FCSTD DOCUMENT  (FreeCAD 0.21R33771 (Git))
Label: mount_on_post
License: All rights reserved
LicenseURL: https://en.wikipedia.org/wiki/All_rights_reserved
objects: App::Link×3, App::DocumentObjectGroup×2, PartDesign::CoordinateSystem×2, App::FeaturePython×1, App::Part×1
note: 2 computed .brp shape members not serialized (recipe doc carries the construction recipe); baked Part::Feature solids carry a one-line shape summary decoded from their .brp
EXTERNAL_REF file=../optomech/postasm/post/RS05P.FCStd obj=LCS_foot
EXTERNAL_REF file=../optomech/postasm/post/RS05P.FCStd obj=Part
EXTERNAL_REF file=../optomech/mounts/mirror/KM05.FCStd obj=LCS_fix_1
EXTERNAL_REF file=../optomech/postasm/post/RS05P.FCStd obj=LCS_top
EXTERNAL_REF file=../optomech/mounts/mirror/KM05.FCStd obj=_177_E0W
EXTERNAL_REF file=../optics/mirrors/BB05.FCStd obj=LCS_Mount
EXTERNAL_REF file=../optomech/mounts/mirror/KM05.FCStd obj=LCS_1
EXTERNAL_REF file=../optics/mirrors/BB05.FCStd obj=BB05
EXTERNAL_REF file=../optics/mirrors/BB05.FCStd obj=Body
EXTERNAL_REF file=../optics/mirrors/BB05.FCStd obj=LCS_opticalCenter

FEATURE [App::DocumentObjectGroup] Parts
FEATURE [PartDesign::CoordinateSystem] LCS_Origin
  AttacherType = Attacher::AttachEngine3D
  MapMode = 2
  Support = -> [X_Axis]
FEATURE [App::DocumentObjectGroup] Constraints
FEATURE [App::FeaturePython] Variables  # WARN: FeaturePython — macro-defined, semantics opaque (R4)
  Type = App::PropertyContainer
FEATURE [App::Link] RS05P
  AttachedBy = #LCS_foot
  AttachedTo = Parent Assembly#LCS_Origin
  LinkPlacement = pos=(-1.8e-15,4e-16,6.35) rot=(1,0,0;1.5708rad)
  LinkedObject = -> <external ../optomech/postasm/post/RS05P.FCStd>#Part
  Placement = pos=(-1.8e-15,4e-16,6.35) rot=(1,0,0;1.5708rad)
  SolverId = Asm4EE
  expr: Placement = LCS_Origin.Placement * AttachmentOffset * RS05P#LCS_foot.Placement ^ -1
FEATURE [App::Link] KM05
  AttachedBy = #LCS_fix_1
  AttachedTo = RS05P#LCS_top
  LinkPlacement = pos=(-1.1477,-9.37337,27.9304) rot=(1,0,0;1.5708rad)
  LinkedObject = -> <external ../optomech/mounts/mirror/KM05.FCStd>#_177_E0W
  Placement = pos=(-1.1477,-9.37337,27.9304) rot=(1,0,0;1.5708rad)
  SolverId = Asm4EE
  expr: Placement = RS05P.Placement * RS05P#LCS_top.Placement * AttachmentOffset * KM05#LCS_fix_1.Placement ^ -1
FEATURE [App::Link] BB05
  AttachedBy = #LCS_Mount
  AttachedTo = KM05#LCS_1
  LinkPlacement = pos=(-2.37e-14,-10.2898,27.432) rot=(1,0,0;1.5708rad)
  LinkedObject = -> <external ../optics/mirrors/BB05.FCStd>#BB05
  Placement = pos=(-2.37e-14,-10.2898,27.432) rot=(1,0,0;1.5708rad)
  SolverId = Asm4EE
  expr: Placement = KM05.Placement * KM05#LCS_1.Placement * AttachmentOffset * BB05#LCS_Mount.Placement ^ -1
FEATURE [PartDesign::CoordinateSystem] Body_LCS_opticalCenter
  AttachedBy = Origin
  AttacherType = Attacher::AttachEngine3D
  Placement = pos=(-2.2e-14,-7.2898,27.432) rot=(-0.57735,0.57735,0.57735;2.0944rad)
  SolverId = Asm4EE
  expr: Placement = BB05.Placement * BB05#Body.Placement * BB05#LCS_opticalCenter.Placement
FEATURE [App::Part] Assembly
  AssemblyType = Part::Link
  Group = -> [LCS_Origin,Constraints,Variables,RS05P,KM05,BB05,Body_LCS_opticalCenter]
  Origin = -> Origin
  Type = Assembly

RESOLVED EXTERNAL PARTS (link-assembly join: the EXTERNAL_REF files above that resolve inside this repo's crawl, each included once):
---- part ../optics/mirrors/BB05.FCStd = doc fcstd_ea6ebc7949ec ----
FCSTD DOCUMENT  (FreeCAD 0.21R33771 (Git))
Label: BB05
License: All rights reserved
LicenseURL: https://en.wikipedia.org/wiki/All_rights_reserved
objects: PartDesign::CoordinateSystem×2, Sketcher::SketchObject×1, PartDesign::Pad×1, PartDesign::Body×1, App::Part×1, Part::FeaturePython×1
note: 7 computed .brp shape members not serialized (recipe doc carries the construction recipe); baked Part::Feature solids carry a one-line shape summary decoded from their .brp

FEATURE [Sketcher::SketchObject] Sketch
  FullyConstrained = true
  MapMode = 5
  Support = -> [XY_Plane001]
  expr: Constraints[1] = 25.4 * 0.5
  sketch-geometry (1):
    g0: Circle CenterX=0 CenterY=0 CenterZ=0 NormalX=0 NormalY=0 NormalZ=1 AngleXU=0 Radius=6.35
  constraints (2):
    c: Coincident(g0,g-1)
    c: Diameter(g0) = 12.7
FEATURE [PartDesign::Pad] Pad
  Direction = (0,0,1)
  Length = 6
  Length2 = 10
  Midplane = true
  Profile = -> Sketch
  ReferenceAxis = -> Sketch [N_Axis]
  Type = 0
FEATURE [PartDesign::CoordinateSystem] LCS_Mount
  AttacherType = Attacher::AttachEngine3D
  MapMode = 11
  Placement = pos=(0,0,-3) rot=(0,0,1;1.5708rad)
  Support = -> [Pad]
FEATURE [PartDesign::CoordinateSystem] LCS_opticalCenter
  AttacherType = Attacher::AttachEngine3D
  MapMode = 11
  Placement = pos=(0,0,-3) rot=(0.707107,-0.707107,0;3.14159rad)
  Support = -> [Pad]
FEATURE [PartDesign::Body] Body  label="mirror"
  Group = -> [Sketch,Pad,LCS_Mount,LCS_opticalCenter]
  Origin = -> Origin001
  Tip = -> Pad
FEATURE [App::Part] BB05
  Group = -> [Body]
  Origin = -> Origin
FEATURE [Part::FeaturePython] Mirror  # WARN: FeaturePython — macro-defined, semantics opaque (R4)
  Base = -> [Body]
  OpticalType = 0
